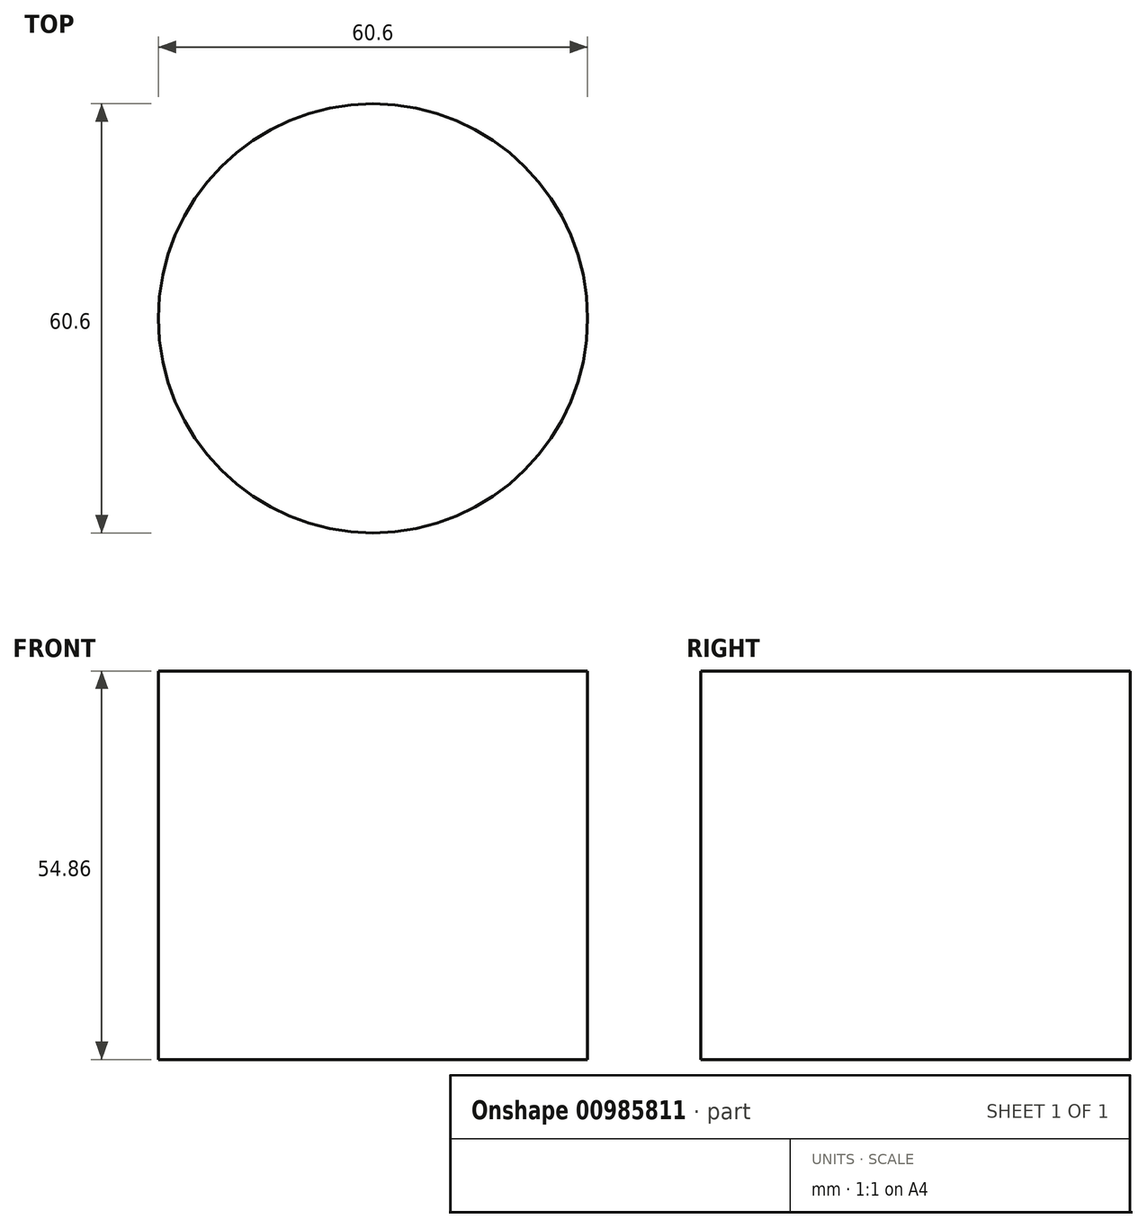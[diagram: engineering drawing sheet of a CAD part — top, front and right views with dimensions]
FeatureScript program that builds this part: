
annotation { "Feature Type Name" : "Feature", "Feature Type Description" : "" }
export const myFeature = defineFeature(function(context is Context, id is Id, definition is map)
    precondition{}
    {
        {
            var Q0;
            Q0=qCreatedBy(makeId("Top.planeOp"),FACE);
            var sketch = newSketch(context, id + "F0", { "sketchPlane" : qUnion([Q0])});
            skCircle(sketch, "E0", {"center": v(0, 0) * mm, "radius": 30.3 * mm});
            skSolve(sketch);
        }
        {
            var Q0;
            Q0 = qSketchRegion(id + "F0", true);
            extrude(context, id + "F1", {"entities" : qUnion([Q0]), "depth" : 54.86 * mm, "offsetDistance" : 25.4 * mm});
        }
    });
